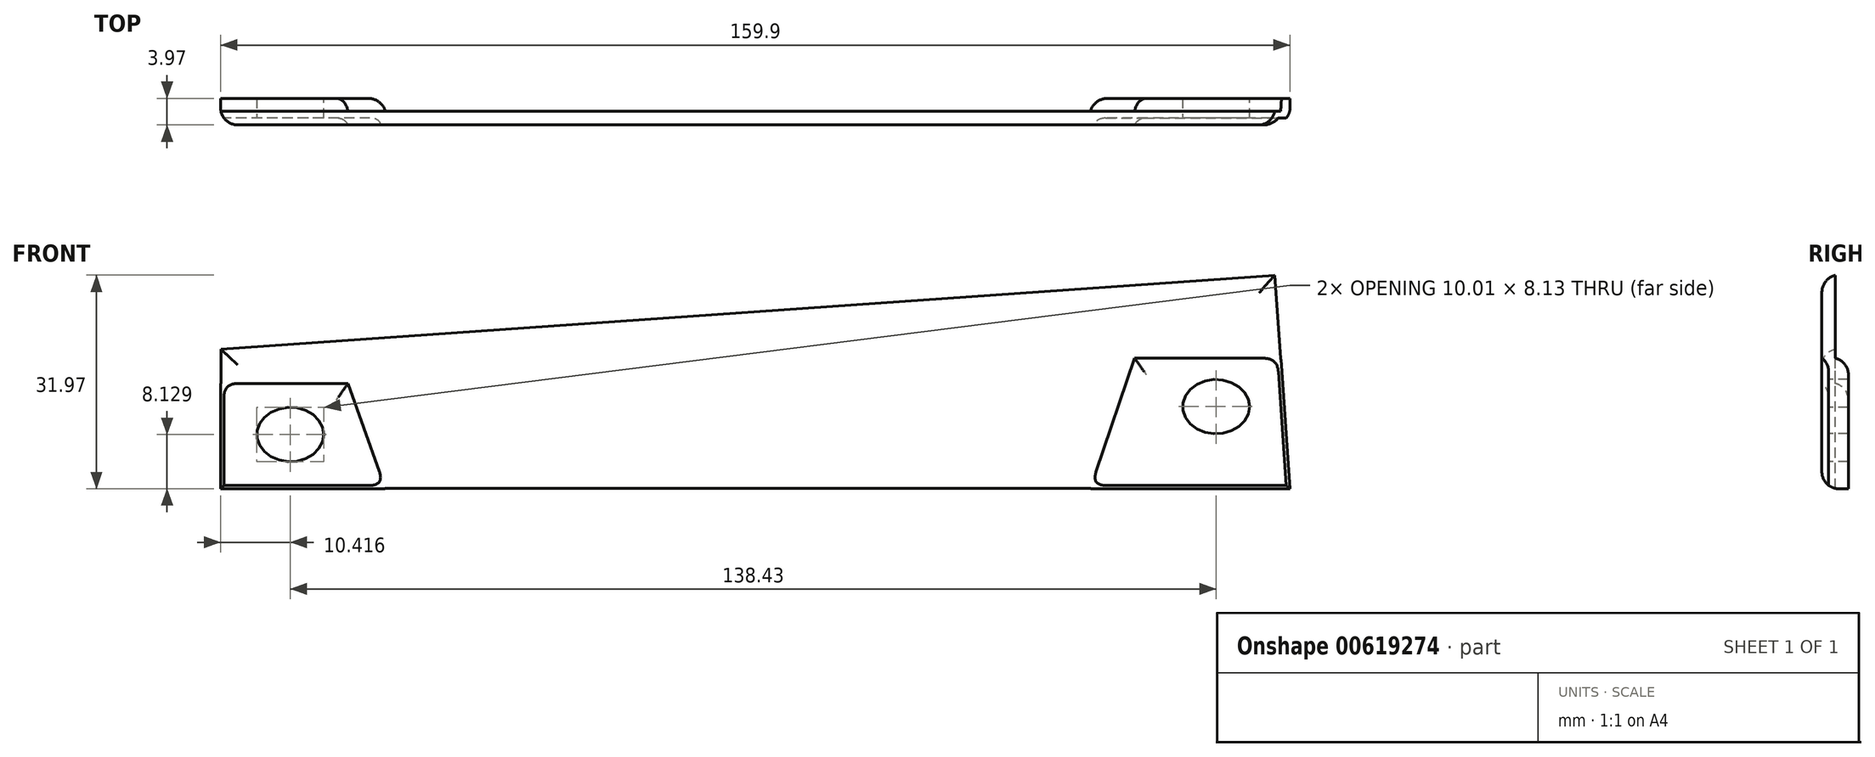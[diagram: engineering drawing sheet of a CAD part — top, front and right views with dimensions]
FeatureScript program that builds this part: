
annotation { "Feature Type Name" : "Feature", "Feature Type Description" : "" }
export const myFeature = defineFeature(function(context is Context, id is Id, definition is map)
    precondition{}
    {
        {
            var Q0;
            Q0=qCreatedBy(makeId("Front.planeOp"),FACE);
            var sketch = newSketch(context, id + "F0", { "sketchPlane" : qUnion([Q0])});
            skLineSegment(sketch, "E0", {"start": v(-60.54, 4.55) * mm, "end": v(-60.54, -18.3) * mm, "construction": true});
            skLineSegment(sketch, "E1", {"start": v(36.48, 11.38) * mm, "end": v(36.48, -18.3) * mm, "construction": true});
            skLineSegment(sketch, "E2", {"start": v(-130, -18.3) * mm, "end": v(154.95, -18.3) * mm, "construction": true});
            skLineSegment(sketch, "E3", {"start": v(-139.87, -1.03) * mm, "end": v(162.35, 20.25) * mm, "construction": true});
            skPoint(sketch, "E4", {"position": v(-78.37, -10.18) * mm});
            skPoint(sketch, "E5", {"position": v(60.06, -6.02) * mm});
            skEllipse(sketch, "E6", {"center": v(-78.37, -10.18) * mm, "majorRadius": 5 * mm, "minorRadius": 4.06 * mm, "majorAxis": v(1, 0)});
            skEllipse(sketch, "E7", {"center": v(60.06, -6.02) * mm, "majorRadius": 5 * mm, "minorRadius": 4.06 * mm, "majorAxis": v(1, 0)});
            skLineSegment(sketch, "E8", {"start": v(-88.79, 2.56) * mm, "end": v(-88.79, -18.3) * mm});
            skLineSegment(sketch, "E9", {"start": v(-88.79, -18.3) * mm, "end": v(71.1, -18.3) * mm});
            skLineSegment(sketch, "E10", {"start": v(71.1, -18.3) * mm, "end": v(68.85, 13.66) * mm});
            skLineSegment(sketch, "E11", {"start": v(68.85, 13.66) * mm, "end": v(-88.79, 2.56) * mm});
            skSolve(sketch);
        }
        {
            var Q0;
            Q0=makeQuery(id+"F0.imprint","IMPRINT",FACE,{"disambiguationData":[TD([[makeQuery(id+"F0.imprint","IMPRINT",EDGE,{"derivedFrom":sQuery(id+"F0.wireOp",EDGE,"E6")}),-1.0]])]});
            extrude(context, id + "F1", {"entities" : qUnion([Q0]), "depth" : 2.03 * mm, "offsetDistance" : 25.4 * mm});
        }
        {
            var Q0;
            Q0=makeQuery(id+"F1.opExtrude","CAP_FACE",FACE,{"disambiguationData":[OSD([sQuery(id+"F0.wireOp",EDGE,"E6"),sQuery(id+"F0.wireOp",EDGE,"E7"),sQuery(id+"F0.wireOp",EDGE,"E8"),sQuery(id+"F0.wireOp",EDGE,"E9"),sQuery(id+"F0.wireOp",EDGE,"E10"),sQuery(id+"F0.wireOp",EDGE,"E11")])],"isStart":false});
            var sketch = newSketch(context, id + "F2", { "sketchPlane" : qUnion([Q0])});
            skLineSegment(sketch, "E12", {"start": v(41.26, -18.3) * mm, "end": v(47.86, 1.22) * mm});
            skLineSegment(sketch, "E13", {"start": v(47.86, 1.22) * mm, "end": v(69.73, 1.22) * mm});
            skEllipse(sketch, "E14.0", {"center": v(60.06, -6.02) * mm, "majorRadius": 5 * mm, "minorRadius": 4.06 * mm, "majorAxis": v(1, 0)});
            skLineSegment(sketch, "E15.0", {"start": v(-88.79, -18.3) * mm, "end": v(-64.15, -18.3) * mm});
            skLineSegment(sketch, "E16.0", {"start": v(71.1, -18.3) * mm, "end": v(69.73, 1.22) * mm});
            skLineSegment(sketch, "E17.0", {"start": v(-88.79, -2.56) * mm, "end": v(-88.79, -18.3) * mm});
            skEllipse(sketch, "E18.0", {"center": v(-78.37, -10.18) * mm, "majorRadius": 5 * mm, "minorRadius": 4.06 * mm, "majorAxis": v(1, 0)});
            skLineSegment(sketch, "E19", {"start": v(-64.15, -18.3) * mm, "end": v(-69.74, -2.56) * mm});
            skLineSegment(sketch, "E20", {"start": v(-69.74, -2.56) * mm, "end": v(-88.79, -2.56) * mm});
            skPoint(sketch, "E21.orphan", {"position": v(-88.79, 2.56) * mm});
            skLineSegment(sketch, "E22.trimOffspring", {"start": v(41.26, -18.3) * mm, "end": v(71.1, -18.3) * mm});
            skPoint(sketch, "E23.orphan", {"position": v(68.85, 13.66) * mm});
            skSolve(sketch);
        }
        {
            var Q0;
            Q0=makeQuery(id+"F2.imprint","IMPRINT",FACE,{"disambiguationData":[TD([[makeQuery(id+"F2.imprint","IMPRINT",EDGE,{"derivedFrom":sQuery(id+"F2.wireOp",EDGE,"E15.0")}),1.0]])]});
            var Q1;
            Q1=makeQuery(id+"F2.imprint","IMPRINT",FACE,{"disambiguationData":[TD([[makeQuery(id+"F2.imprint","IMPRINT",EDGE,{"derivedFrom":sQuery(id+"F2.wireOp",EDGE,"E12")}),-1.0]])]});
            extrude(context, id + "F3", {"entities" : qUnion([Q0, Q1]), "operationType" : NewBodyOperationType.ADD, "oppositeDirection" : true, "depth" : 3.98 * mm, "offsetDistance" : 25.4 * mm});
        }
        {
            var Q0;
            Q0 = qSketchRegion(id + "F2", true);
            extrude(context, id + "F4", {"entities" : qUnion([Q0]), "operationType" : NewBodyOperationType.REMOVE, "oppositeDirection" : true, "depth" : 1.02 * mm, "offsetDistance" : 25.4 * mm});
        }
        {
            var Q0;
            Q0=makeQuery(id+"F3.opExtrude","CAP_EDGE",EDGE,{"disambiguationData":[OSD([sQuery(id+"F2.wireOp",EDGE,"E20")])],"isStart":false});
            var Q1;
            Q1=makeQuery(id+"F3.opExtrude","CAP_EDGE",EDGE,{"disambiguationData":[OSD([sQuery(id+"F2.wireOp",EDGE,"E19")])],"isStart":false});
            var Q2;
            Q2=makeQuery(id+"F3.opExtrude","CAP_EDGE",EDGE,{"disambiguationData":[OSD([sQuery(id+"F2.wireOp",EDGE,"E12")])],"isStart":false});
            var Q3;
            Q3=makeQuery(id+"F3.opExtrude","CAP_EDGE",EDGE,{"disambiguationData":[OSD([sQuery(id+"F2.wireOp",EDGE,"E13")])],"isStart":false});
            fillet(context, id + "F5", {"entities" : qUnion([Q0, Q1, Q2, Q3]), "radius" : 2.54 * mm, "tangentPropagation" : true, "allowEdgeOverflow" : false});
        }
        {
            var Q0;
            Q0=makeQuery(id+"F1.opExtrude","CAP_EDGE",EDGE,{"disambiguationData":[OSD([sQuery(id+"F0.wireOp",EDGE,"E9")])],"isStart":false});
            var Q1;
            Q1=makeQuery(id+"F1.opExtrude","CAP_EDGE",EDGE,{"disambiguationData":[OSD([sQuery(id+"F0.wireOp",EDGE,"E10")])],"isStart":false});
            var Q2;
            Q2=makeQuery(id+"F1.opExtrude","CAP_EDGE",EDGE,{"disambiguationData":[OSD([sQuery(id+"F0.wireOp",EDGE,"E11")])],"isStart":false});
            var Q3;
            Q3=makeQuery(id+"F1.opExtrude","CAP_EDGE",EDGE,{"disambiguationData":[OSD([sQuery(id+"F0.wireOp",EDGE,"E8")])],"isStart":false});
            fillet(context, id + "F6", {"entities" : qUnion([Q0, Q1, Q2, Q3]), "radius" : 2.54 * mm, "tangentPropagation" : true, "allowEdgeOverflow" : false});
        }
        {
            var Q0;
            Q0=makeQuery(id+"F4.boolean.opBoolean","COPY",EDGE,{"derivedFrom":makeQuery(id+"F4.opExtrude","CAP_EDGE",EDGE,{"disambiguationData":[OSD([sQuery(id+"F2.wireOp",EDGE,"E12")])],"isStart":false})});
            var Q1;
            Q1=makeQuery(id+"F4.boolean.opBoolean","COPY",EDGE,{"derivedFrom":makeQuery(id+"F4.opExtrude","CAP_EDGE",EDGE,{"disambiguationData":[OSD([sQuery(id+"F2.wireOp",EDGE,"E13")])],"isStart":false})});
            var Q2;
            Q2=makeQuery(id+"F4.boolean.opBoolean","COPY",EDGE,{"derivedFrom":makeQuery(id+"F4.opExtrude","CAP_EDGE",EDGE,{"disambiguationData":[OSD([sQuery(id+"F2.wireOp",EDGE,"E20")])],"isStart":false})});
            var Q3;
            Q3=makeQuery(id+"F4.boolean.opBoolean","COPY",EDGE,{"derivedFrom":makeQuery(id+"F4.opExtrude","CAP_EDGE",EDGE,{"disambiguationData":[OSD([sQuery(id+"F2.wireOp",EDGE,"E19")])],"isStart":false})});
            fillet(context, id + "F7", {"entities" : qUnion([Q0, Q1, Q2, Q3]), "radius" : 2.54 * mm, "tangentPropagation" : true, "allowEdgeOverflow" : false});
        }
    });
